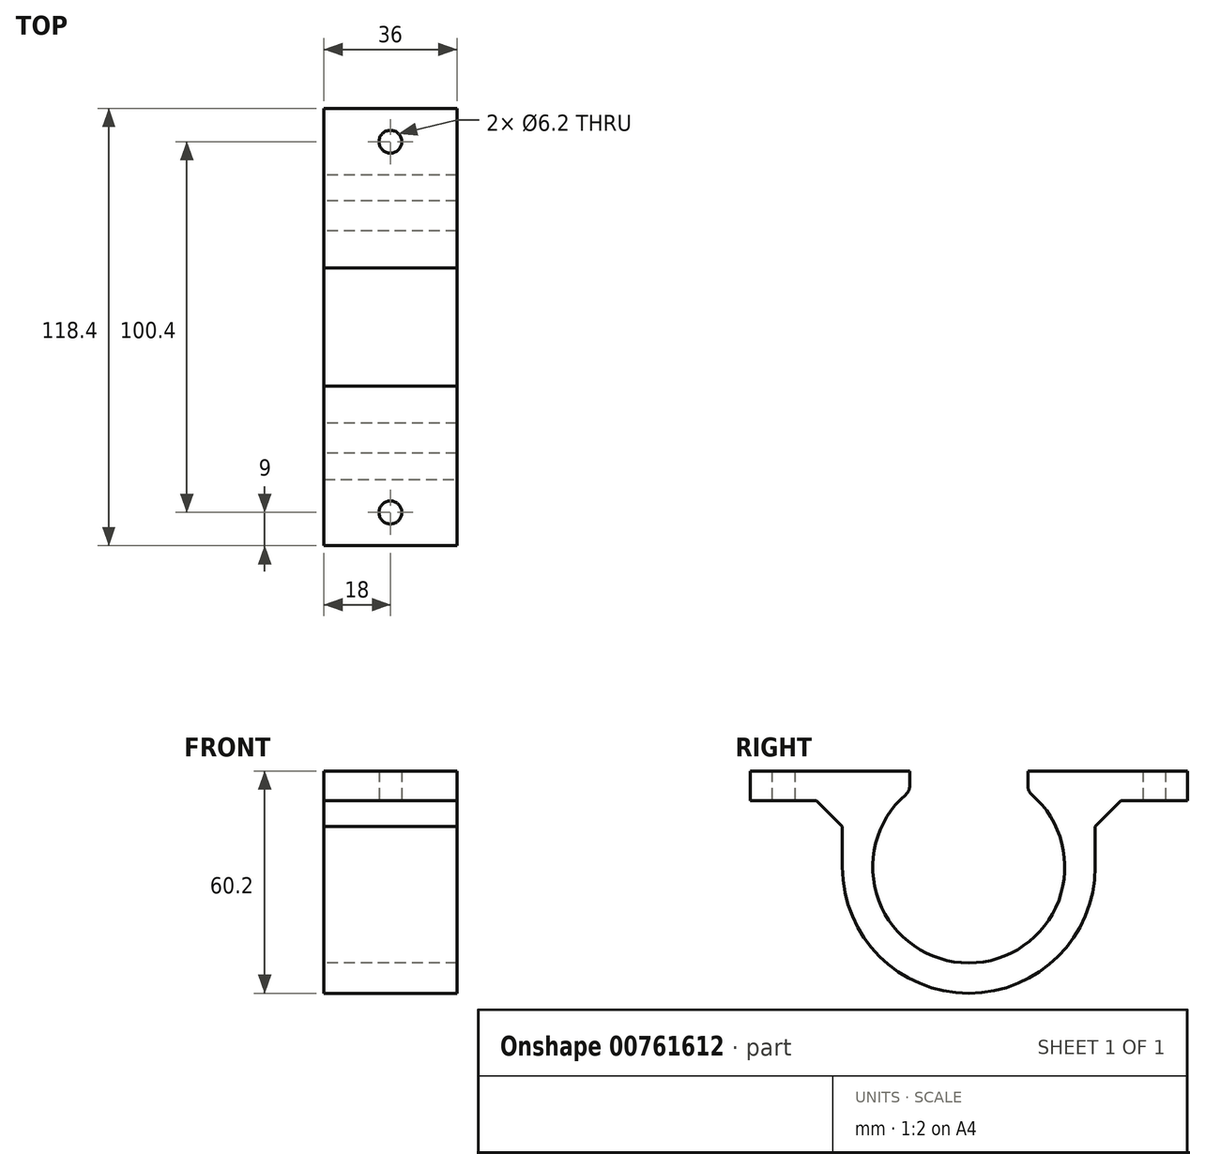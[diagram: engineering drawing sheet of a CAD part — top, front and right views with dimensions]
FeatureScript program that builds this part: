
annotation { "Feature Type Name" : "Feature", "Feature Type Description" : "" }
export const myFeature = defineFeature(function(context is Context, id is Id, definition is map)
    precondition{}
    {
        {
            var Q0;
            Q0=qCreatedBy(makeId("Right.planeOp"),FACE);
            var sketch = newSketch(context, id + "F0", { "sketchPlane" : qUnion([Q0])});
            skCircle(sketch, "E0", {"center": v(0, 0) * mm, "radius": 26 * mm, "construction": true});
            skLineSegment(sketch, "E1", {"start": v(26, 0) * mm, "end": v(26, 26) * mm, "construction": true});
            skLineSegment(sketch, "E2", {"start": v(26, 26) * mm, "end": v(-26, 26) * mm, "construction": true});
            skLineSegment(sketch, "E3", {"start": v(-26, 26) * mm, "end": v(-26, 0) * mm, "construction": true});
            skLineSegment(sketch, "E4", {"start": v(-26, 0) * mm, "end": v(26, 0) * mm, "construction": true});
            skLineSegment(sketch, "E5", {"start": v(-26, 26) * mm, "end": v(-59.2, 26) * mm});
            skLineSegment(sketch, "E6", {"start": v(-59.2, 26) * mm, "end": v(-59.2, 18) * mm});
            skLineSegment(sketch, "E7", {"start": v(-59.2, 18) * mm, "end": v(-34.2, 18) * mm});
            skLineSegment(sketch, "E8", {"start": v(-34.2, 18) * mm, "end": v(-34.2, 0) * mm});
            skLineSegment(sketch, "E9", {"start": v(26, 26) * mm, "end": v(59.2, 26) * mm});
            skLineSegment(sketch, "E10", {"start": v(59.2, 26) * mm, "end": v(59.2, 18) * mm});
            skLineSegment(sketch, "E11", {"start": v(59.2, 18) * mm, "end": v(34.2, 18) * mm});
            skLineSegment(sketch, "E12", {"start": v(34.2, 18) * mm, "end": v(34.2, 0) * mm});
            skArc(sketch, "E13", {"start": v(-34.2, 0) * mm, "mid": v(0, -34.2) * mm, "end": v(34.2, 0) * mm});
            skArc(sketch, "E14", {"start": v(-26, 0) * mm, "mid": v(0, -26) * mm, "end": v(26, 0) * mm});
            skLineSegment(sketch, "E15", {"start": v(-46.7, 18) * mm, "end": v(-46.7, 26) * mm, "construction": true});
            skLineSegment(sketch, "E16", {"start": v(46.7, 18) * mm, "end": v(46.7, 26) * mm, "construction": true});
            skLineSegment(sketch, "E17", {"start": v(34.2, 18) * mm, "end": v(34.2, 26) * mm, "construction": true});
            skLineSegment(sketch, "E18", {"start": v(-34.2, 18) * mm, "end": v(-34.2, 26) * mm, "construction": true});
            skArc(sketch, "E19", {"start": v(26, 0) * mm, "mid": v(23.37, 11.4) * mm, "end": v(16, 20.5) * mm});
            skLineSegment(sketch, "E20", {"start": v(26, 26) * mm, "end": v(16, 26) * mm});
            skLineSegment(sketch, "E21", {"start": v(16, 26) * mm, "end": v(16, 20.5) * mm});
            skArc(sketch, "E22", {"start": v(-26, 0) * mm, "mid": v(-23.37, 11.4) * mm, "end": v(-16, 20.5) * mm});
            skLineSegment(sketch, "E23", {"start": v(16, 20.5) * mm, "end": v(-16, 20.5) * mm, "construction": true});
            skLineSegment(sketch, "E24", {"start": v(-16, 20.5) * mm, "end": v(-16, 26) * mm});
            skLineSegment(sketch, "E25", {"start": v(-16, 26) * mm, "end": v(-26, 26) * mm});
            skSolve(sketch);
        }
        {
            var Q0;
            Q0=makeQuery(id+"F0.imprint","IMPRINT",FACE,{"disambiguationData":[TD([[makeQuery(id+"F0.imprint","IMPRINT",EDGE,{"derivedFrom":sQuery(id+"F0.wireOp",EDGE,"E5")}),1.0]])]});
            extrude(context, id + "F1", {"entities" : qUnion([Q0]), "depth" : 36 * mm, "offsetDistance" : 25 * mm});
        }
        {
            var Q0;
            Q0=makeQuery(id+"F1.opExtrude","SWEPT_FACE",FACE,{"disambiguationData":[OSD([sQuery(id+"F0.wireOp",EDGE,"E7")])]});
            var sketch = newSketch(context, id + "F2", { "sketchPlane" : qUnion([Q0])});
            skLineSegment(sketch, "E26", {"start": v(36, 50.2) * mm, "end": v(0, 50.2) * mm, "construction": true});
            skCircle(sketch, "E27", {"center": v(18, 50.2) * mm, "radius": 3.1 * mm});
            skLineSegment(sketch, "E28", {"start": v(36, -50.2) * mm, "end": v(0, -50.2) * mm, "construction": true});
            skCircle(sketch, "E29", {"center": v(18, -50.2) * mm, "radius": 3.1 * mm});
            skCircle(sketch, "E30", {"center": v(18, 50.2) * mm, "radius": 9 * mm, "construction": true});
            skCircle(sketch, "E31", {"center": v(18, -50.2) * mm, "radius": 9 * mm, "construction": true});
            skSolve(sketch);
        }
        {
            var Q0;
            Q0 = qSketchRegion(id + "F2", true);
            extrude(context, id + "F3", {"entities" : qUnion([Q0]), "operationType" : NewBodyOperationType.REMOVE, "endBound" : BoundingType.THROUGH_ALL, "oppositeDirection" : true, "depth" : 25 * mm, "offsetDistance" : 25 * mm});
        }
        {
            var Q0;
            Q0=makeQuery(id+"F1.opExtrude","SWEPT_EDGE",EDGE,{"disambiguationData":[OSD([sQuery(id+"F0.wireOp",EDGE,"E7"),sQuery(id+"F0.wireOp",EDGE,"E8")])]});
            var Q1;
            Q1=makeQuery(id+"F1.opExtrude","SWEPT_EDGE",EDGE,{"disambiguationData":[OSD([sQuery(id+"F0.wireOp",EDGE,"E11"),sQuery(id+"F0.wireOp",EDGE,"E12")])]});
            chamfer(context, id + "F4", {"entities" : qUnion([Q0, Q1]), "width" : 7 * mm, "tangentPropagation" : true});
        }
        {
            var Q0;
            Q0=makeQuery(id+"F1.opExtrude","SWEPT_EDGE",EDGE,{"disambiguationData":[OSD([sQuery(id+"F0.wireOp",EDGE,"E19"),sQuery(id+"F0.wireOp",EDGE,"E21")])]});
            var Q1;
            Q1=makeQuery(id+"F1.opExtrude","SWEPT_EDGE",EDGE,{"disambiguationData":[OSD([sQuery(id+"F0.wireOp",EDGE,"E22"),sQuery(id+"F0.wireOp",EDGE,"E24")])]});
            fillet(context, id + "F5", {"entities" : qUnion([Q0, Q1]), "radius" : 3 * mm, "tangentPropagation" : true, "allowEdgeOverflow" : false});
        }
    });
